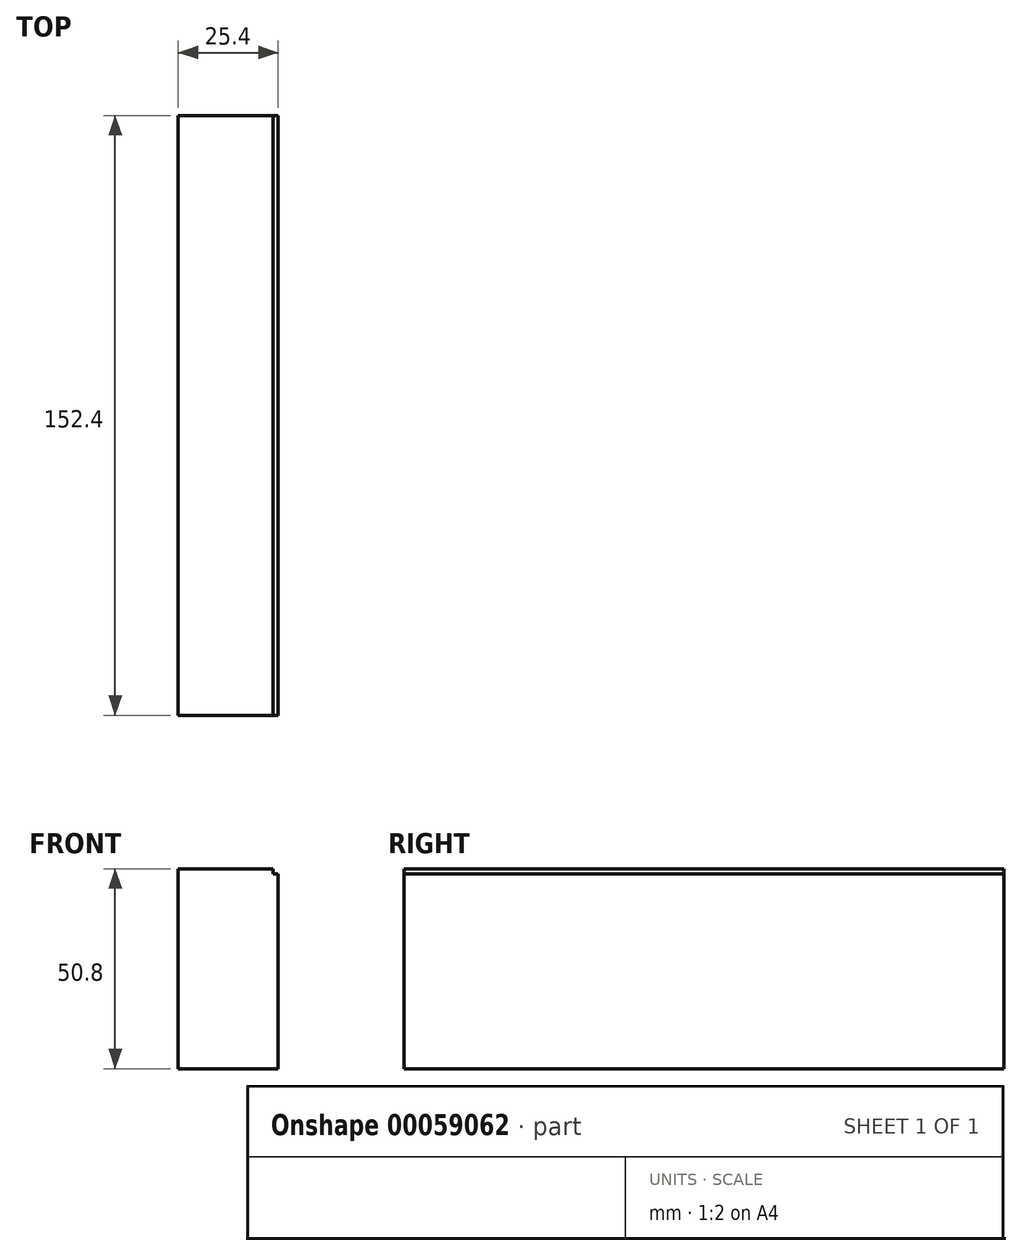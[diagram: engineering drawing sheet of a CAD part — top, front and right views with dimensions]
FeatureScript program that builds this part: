
annotation { "Feature Type Name" : "Feature", "Feature Type Description" : "" }
export const myFeature = defineFeature(function(context is Context, id is Id, definition is map)
    precondition{}
    {
        {
            var Q0;
            Q0=qCreatedBy(makeId("Top.planeOp"),FACE);
            var sketch = newSketch(context, id + "F0", { "sketchPlane" : qUnion([Q0])});
            skLineSegment(sketch, "E0.bottom", {"start": v(11.07, -74.6) * mm, "end": v(36.47, -74.6) * mm});
            skLineSegment(sketch, "E0.top", {"start": v(11.07, 77.8) * mm, "end": v(36.47, 77.8) * mm});
            skLineSegment(sketch, "E0.left", {"start": v(11.07, -74.6) * mm, "end": v(11.07, 77.8) * mm});
            skLineSegment(sketch, "E0.right", {"start": v(36.47, -74.6) * mm, "end": v(36.47, 77.8) * mm});
            skLineSegment(sketch, "E1", {"start": v(35.2, 77.8) * mm, "end": v(35.2, -74.6) * mm, "construction": true});
            skCircle(sketch, "E2", {"center": v(39.96, 47.75) * mm, "radius": 4.76 * mm, "construction": true});
            skCircle(sketch, "E3", {"center": v(38.37, 24.07) * mm, "radius": 3.18 * mm, "construction": true});
            skLineSegment(sketch, "E4", {"start": v(39.96, 47.75) * mm, "end": v(36.47, 47.75) * mm, "construction": true});
            skLineSegment(sketch, "E5", {"start": v(38.37, 24.07) * mm, "end": v(36.47, 24.07) * mm, "construction": true});
            skSolve(sketch);
        }
        {
            var Q0;
            Q0=makeQuery(id+"F0.imprint","IMPRINT",FACE,{"disambiguationData":[TD([[makeQuery(id+"F0.imprint","IMPRINT",EDGE,{"derivedFrom":sQuery(id+"F0.wireOp",EDGE,"E0.bottom")}),1.0]])]});
            extrude(context, id + "F1", {"entities" : qUnion([Q0]), "depth" : 50.8 * mm});
        }
        {
            var Q0;
            Q0=makeQuery(id+"F1.opExtrude","CAP_FACE",FACE,{"disambiguationData":[OSD([sQuery(id+"F0.wireOp",EDGE,"E0.bottom"),sQuery(id+"F0.wireOp",EDGE,"E0.top"),sQuery(id+"F0.wireOp",EDGE,"E0.left"),sQuery(id+"F0.wireOp",EDGE,"E0.right")])],"isStart":false});
            var sketch = newSketch(context, id + "F2", { "sketchPlane" : qUnion([Q0])});
            skLineSegment(sketch, "E6.0", {"start": v(35.2, 77.8) * mm, "end": v(35.2, -74.6) * mm});
            skSolve(sketch);
        }
        {
            var Q0;
            {var subQ0=sQuery(id+"F2.wireOp",EDGE,"E6.0");Q0=makeQuery(id+"F2.imprint","IMPRINT",FACE,{"disambiguationData":[TD([[makeQuery(id+"F2.imprint","IMPRINT",EDGE,{"derivedFrom":subQ0}),1.0]])]});}
            extrude(context, id + "F3", {"entities" : qUnion([Q0]), "operationType" : NewBodyOperationType.REMOVE, "oppositeDirection" : true, "depth" : 1.27 * mm});
        }
    });
